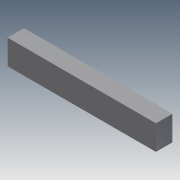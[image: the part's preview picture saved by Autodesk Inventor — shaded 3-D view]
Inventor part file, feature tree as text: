
AUTODESK INVENTOR PART (.ipt)
format: ipt  version: 2011 (Build 150239000, 239)  size: 66,048 bytes
history: native  units: in
note: dims shown in document units (in); Inventor stores cm internally (conversion verified against a paired STEP export)
features: extrude x1, sketch x1
ambient origin geometry x8: Origin, YZ Plane, XZ Plane, XY Plane, X Axis, Y Axis, Z Axis, Center Point
bodies: Solid1 (feature_tree)
feature tree (2):
  extrude  "Extrusion1"  Depth=3.0in
  sketch  "Sketch1"  dims[d0=18.0in d1=3.0in d2=2.0in d3=0.0in]
